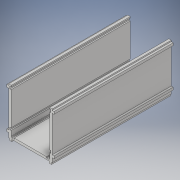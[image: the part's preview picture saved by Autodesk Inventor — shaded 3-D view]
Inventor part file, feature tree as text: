
AUTODESK INVENTOR PART (.ipt)
format: ipt  version: 2017 (Build 210142000, 142)  size: 179,712 bytes
history: native  units: in
note: dims shown in document units (in); Inventor stores cm internally (conversion verified against a paired STEP export)
features: extrude x1, sketch x1
ambient origin geometry x8: Origin, YZ Plane, XZ Plane, XY Plane, X Axis, Y Axis, Z Axis, Center Point
bodies: Solid1 (feature_tree)
feature tree (2):
  extrude  "Extrusion1"  Depth=4.375in
  sketch  "Sketch1"  dims[d0=4.6875in d1=4.375in d2=0.25in d3=4.4375in d4=3.875in d5=12.0in d6=0.0in d7=4.6875in d8=0.125in d9=0.125in d10=0.125in d11=0.188in d12=0.25in d13=0.438in d14=0.188in d15=0.25in d16=0.0625in d17=0.188in d18=0.25in d19=0.188in d20=0.188in d21=0.0625in d22=0.25in d23=0.25in d24=0.125in d25=0.125in d26=0.5in d27=0.25in d28=0.0625in d29=0.125in d30=0.25in d31=0.0625in d32=0.25in d33=0.5in d34=0.25in]
